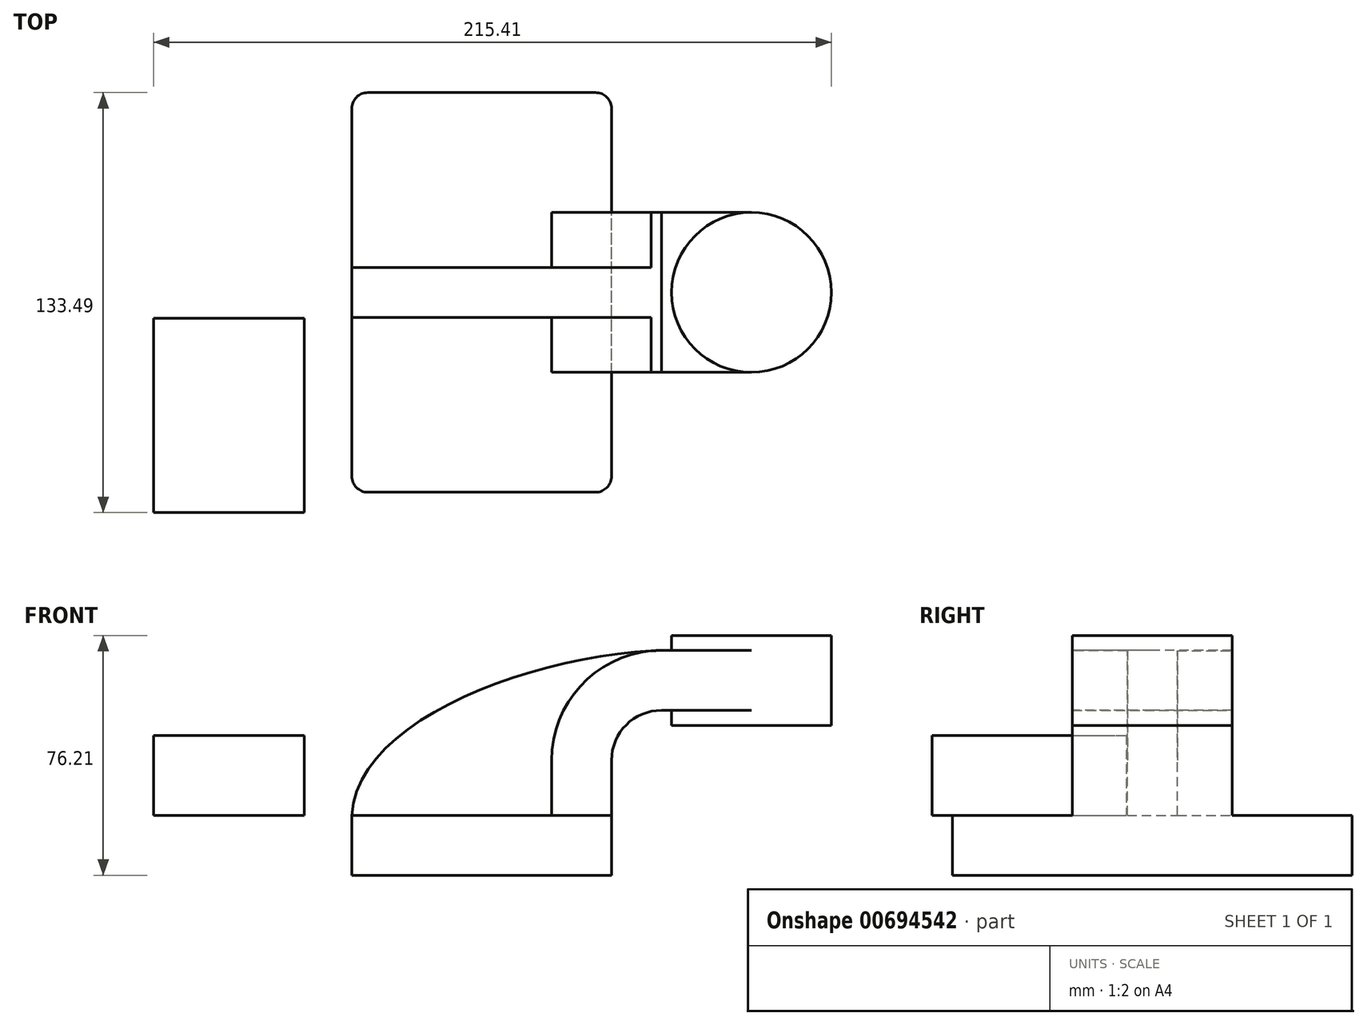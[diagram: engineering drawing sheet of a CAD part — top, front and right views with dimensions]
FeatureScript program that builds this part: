
annotation { "Feature Type Name" : "Feature", "Feature Type Description" : "" }
export const myFeature = defineFeature(function(context is Context, id is Id, definition is map)
    precondition{}
    {
        {
            var Q0;
            Q0=qCreatedBy(makeId("Front.planeOp"),FACE);
            var sketch = newSketch(context, id + "F0", { "sketchPlane" : qUnion([Q0])});
            skLineSegment(sketch, "E0.rect.bottom", {"start": v(-41.28, 9.52) * mm, "end": v(41.28, 9.52) * mm});
            skLineSegment(sketch, "E0.rect.top", {"start": v(-41.28, -9.52) * mm, "end": v(41.28, -9.52) * mm});
            skLineSegment(sketch, "E0.rect.left", {"start": v(-41.28, 9.52) * mm, "end": v(-41.28, -9.52) * mm});
            skLineSegment(sketch, "E0.rect.right", {"start": v(41.28, 9.52) * mm, "end": v(41.28, -9.52) * mm});
            skPoint(sketch, "E0.rect.middle", {"position": v(0, 0) * mm});
            skLineSegment(sketch, "E1", {"start": v(41.28, 9.52) * mm, "end": v(41.28, 27) * mm});
            skArc(sketch, "E2", {"start": v(41.28, 27) * mm, "mid": v(45.92, 38.23) * mm, "end": v(57.15, 42.88) * mm});
            skLineSegment(sketch, "E3", {"start": v(57.15, 42.88) * mm, "end": v(85.72, 42.88) * mm});
            skLineSegment(sketch, "E4.rect.bottom", {"start": v(60.32, 38.1) * mm, "end": v(111.12, 38.1) * mm});
            skLineSegment(sketch, "E4.rect.top", {"start": v(60.32, 66.68) * mm, "end": v(111.12, 66.68) * mm});
            skLineSegment(sketch, "E4.rect.left", {"start": v(60.32, 38.1) * mm, "end": v(60.32, 66.68) * mm});
            skLineSegment(sketch, "E4.rect.right", {"start": v(111.13, 38.1) * mm, "end": v(111.12, 66.68) * mm});
            skPoint(sketch, "E4.rect.middle", {"position": v(85.72, 52.39) * mm});
            skLineSegment(sketch, "E5.0", {"start": v(57.15, 61.93) * mm, "end": v(85.72, 61.93) * mm});
            skArc(sketch, "E5.1", {"start": v(22.23, 27) * mm, "mid": v(32.45, 51.7) * mm, "end": v(57.15, 61.93) * mm});
            skLineSegment(sketch, "E5.2", {"start": v(22.23, 9.52) * mm, "end": v(22.23, 27) * mm});
            skLineSegment(sketch, "E6", {"start": v(85.72, 38.1) * mm, "end": v(85.72, 66.68) * mm});
            skFitSpline(sketch, "E7", {"points": [v(-41.28, 9.53) * mm, v(57.15, 61.93) * mm], "startDerivative": vector(5.2, 92.34) * mm, "endDerivative": vector(120.92, 4.22) * mm});
            skSolve(sketch);
        }
        {
            var Q0;
            Q0=makeQuery(id+"F0.imprint","IMPRINT",FACE,{"disambiguationData":[TD([[makeQuery(id+"F0.imprint","IMPRINT",EDGE,{"derivedFrom":sQuery(id+"F0.wireOp",EDGE,"E0.rect.top")}),1.0]])]});
            extrude(context, id + "F1", {"entities" : qUnion([Q0]), "endBound" : BoundingType.SYMMETRIC, "depth" : 127 * mm});
        }
        {
            var Q0;
            {var subQ9=sQuery(id+"F0.wireOp",EDGE,"E1");Q0=makeQuery(id+"F0.imprint","IMPRINT",FACE,{"disambiguationData":[TD([[makeQuery(id+"F0.imprint","IMPRINT",EDGE,{"derivedFrom":subQ9}),1.0]])]});}
            var Q1;
            {var subQ0=sQuery(id+"F0.wireOp",EDGE,"E6");var subQ1=sQuery(id+"F0.wireOp",EDGE,"E3");var subQ2=makeQuery(id+"F0.imprint","INTERSECT",VERTEX,{"derivedFrom":[subQ1,subQ0]});Q1=makeQuery(id+"F0.imprint","IMPRINT",FACE,{"disambiguationData":[TD([[makeQuery(id+"F0.imprint","IMPRINT",EDGE,{"disambiguationData":[TD([[subQ2,1.0]])],"derivedFrom":subQ1}),1.0]])]});}
            extrude(context, id + "F2", {"entities" : qUnion([Q0, Q1]), "operationType" : NewBodyOperationType.ADD, "endBound" : BoundingType.SYMMETRIC, "depth" : 50.8 * mm});
        }
        {
            var Q0;
            {var subQ3=sQuery(id+"F0.wireOp",EDGE,"E5.2");Q0=makeQuery(id+"F0.imprint","IMPRINT",FACE,{"disambiguationData":[TD([[makeQuery(id+"F0.imprint","IMPRINT",EDGE,{"derivedFrom":subQ3}),1.0]])]});}
            extrude(context, id + "F3", {"entities" : qUnion([Q0]), "operationType" : NewBodyOperationType.ADD, "endBound" : BoundingType.SYMMETRIC, "depth" : 15.88 * mm});
        }
        {
            var Q0;
            {var subQ5=sQuery(id+"F0.wireOp",EDGE,"E4.rect.right");Q0=makeQuery(id+"F0.imprint","IMPRINT",FACE,{"disambiguationData":[TD([[makeQuery(id+"F0.imprint","IMPRINT",EDGE,{"derivedFrom":subQ5}),1.0]])]});}
            var Q1;
            Q1=sQuery(id+"F0.wireOp",EDGE,"E6");
            revolve(context, id + "F4", {"operationType" : NewBodyOperationType.ADD, "entities" : qUnion([Q0]), "axis" : qUnion([Q1]), "revolveType" : RevolveType.FULL});
        }
        {
            var Q0;
            Q0=makeQuery(id+"F1.opExtrude","CAP_EDGE",EDGE,{"disambiguationData":[OSD([sQuery(id+"F0.wireOp",EDGE,"E0.rect.right")])],"isStart":false});
            var Q1;
            Q1=makeQuery(id+"F1.opExtrude","CAP_EDGE",EDGE,{"disambiguationData":[OSD([sQuery(id+"F0.wireOp",EDGE,"E0.rect.left")])],"isStart":false});
            var Q2;
            Q2=makeQuery(id+"F1.opExtrude","CAP_EDGE",EDGE,{"disambiguationData":[OSD([sQuery(id+"F0.wireOp",EDGE,"E0.rect.right")])],"isStart":true});
            var Q3;
            Q3=makeQuery(id+"F1.opExtrude","CAP_EDGE",EDGE,{"disambiguationData":[OSD([sQuery(id+"F0.wireOp",EDGE,"E0.rect.left")])],"isStart":true});
            fillet(context, id + "F5", {"entities" : qUnion([Q0, Q1, Q2, Q3]), "radius" : 5.08 * mm, "tangentPropagation" : true, "allowEdgeOverflow" : false});
        }
        {
            var Q0;
            {var subQ4=sQuery(id+"F0.wireOp",EDGE,"E0.rect.bottom");var subQ5=sQuery(id+"F0.wireOp",EDGE,"E0.rect.right");var subQ6=sQuery(id+"F0.wireOp",EDGE,"E0.rect.left");Q0=makeQuery(id+"F3.boolean.opBoolean","SPLIT",FACE,{"disambiguationData":[TD([makeQuery(id+"F1.opExtrude","CAP_FACE",FACE,{"disambiguationData":[OSD([subQ4,sQuery(id+"F0.wireOp",EDGE,"E0.rect.top"),subQ6,subQ5])],"isStart":false})])],"derivedFrom":makeQuery(id+"F1.opExtrude","SWEPT_FACE",FACE,{"disambiguationData":[OSD([subQ4])]})});}
            var sketch = newSketch(context, id + "F6", { "sketchPlane" : qUnion([Q0])});
            skLineSegment(sketch, "E8.bottom", {"start": v(-104.28, -70) * mm, "end": v(-56.35, -70) * mm});
            skLineSegment(sketch, "E8.top", {"start": v(-104.28, -8.26) * mm, "end": v(-56.35, -8.26) * mm});
            skLineSegment(sketch, "E8.left", {"start": v(-104.28, -70) * mm, "end": v(-104.28, -8.26) * mm});
            skLineSegment(sketch, "E8.right", {"start": v(-56.35, -70) * mm, "end": v(-56.35, -8.26) * mm});
            skSolve(sketch);
        }
        {
            var Q0;
            Q0=makeQuery(id+"F6.imprint","IMPRINT",FACE,{"disambiguationData":[TD([[makeQuery(id+"F6.imprint","IMPRINT",EDGE,{"derivedFrom":sQuery(id+"F6.wireOp",EDGE,"E8.bottom")}),1.0]])]});
            extrude(context, id + "F7", {"entities" : qUnion([Q0]), "depth" : 25.4 * mm, "offsetDistance" : 25.4 * mm});
        }
    });
